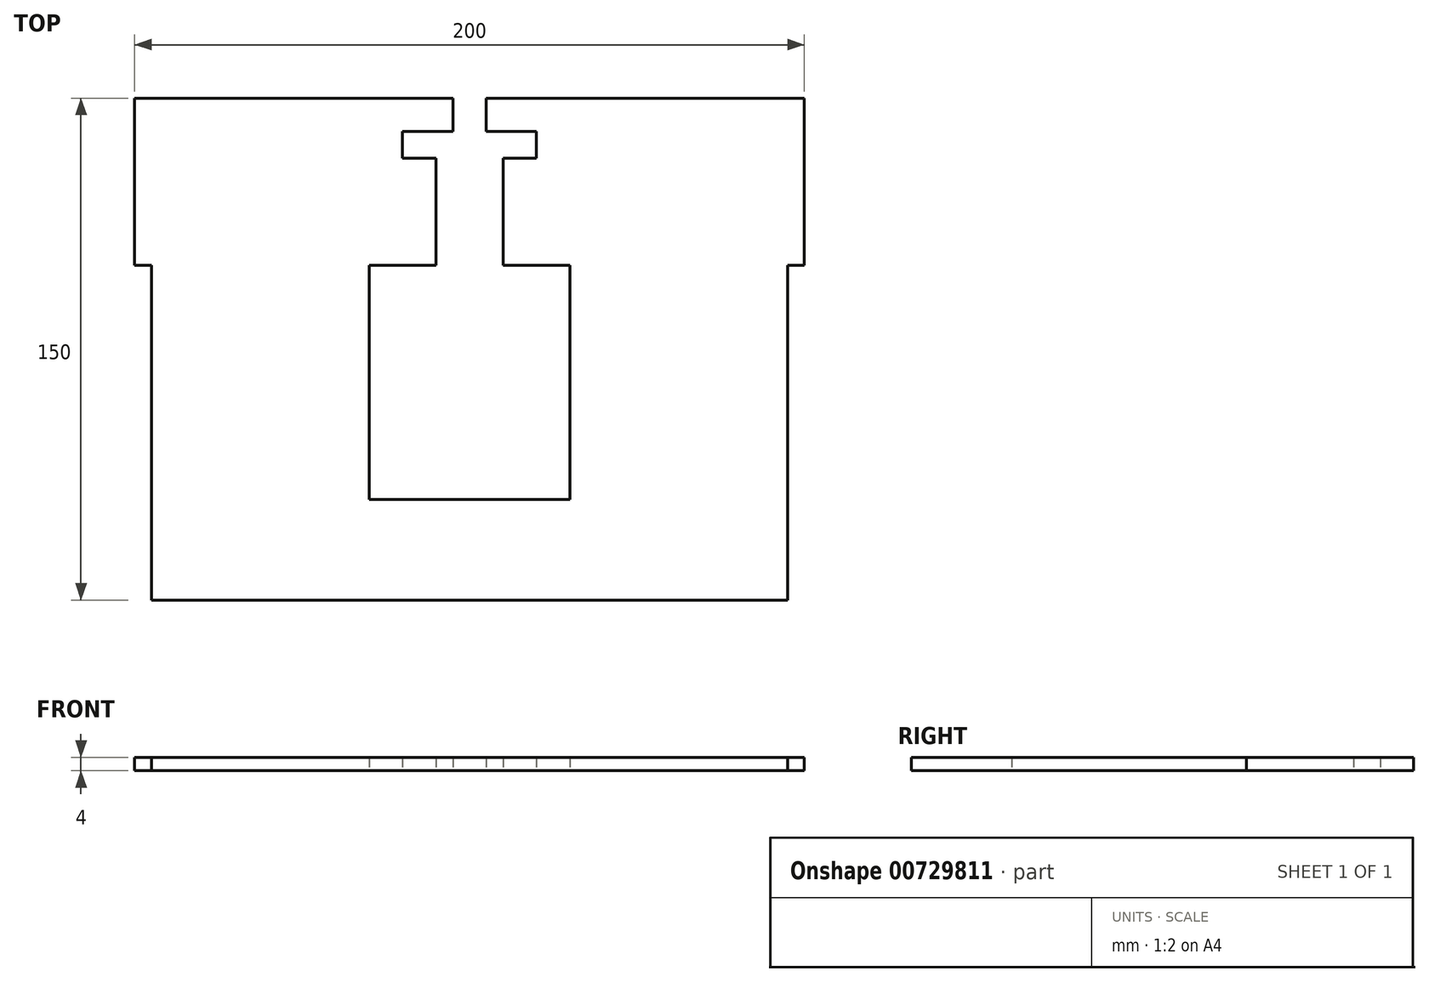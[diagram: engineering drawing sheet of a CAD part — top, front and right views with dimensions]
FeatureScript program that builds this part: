
annotation { "Feature Type Name" : "Feature", "Feature Type Description" : "" }
export const myFeature = defineFeature(function(context is Context, id is Id, definition is map)
    precondition{}
    {
        {
            var Q0;
            Q0=qCreatedBy(makeId("Top.planeOp"),FACE);
            var sketch = newSketch(context, id + "F0", { "sketchPlane" : qUnion([Q0])});
            skLineSegment(sketch, "E0.bottom", {"start": v(20, -10) * mm, "end": v(5, -10) * mm});
            skLineSegment(sketch, "E0.left", {"start": v(20, -10) * mm, "end": v(20, -18) * mm});
            skLineSegment(sketch, "E0.right", {"start": v(-20, -10) * mm, "end": v(-20, -18) * mm});
            skPoint(sketch, "E0.middle", {"position": v(0, 0) * mm});
            skLineSegment(sketch, "E1.top", {"start": v(-100, 0) * mm, "end": v(-5, 0) * mm});
            skLineSegment(sketch, "E1.left", {"start": v(-100, -50) * mm, "end": v(-100, 0) * mm});
            skLineSegment(sketch, "E1.right", {"start": v(100, -50) * mm, "end": v(100, 0) * mm});
            skLineSegment(sketch, "E2", {"start": v(-30, -50) * mm, "end": v(-30, -120) * mm});
            skLineSegment(sketch, "E3", {"start": v(30, -50) * mm, "end": v(30, -120) * mm});
            skLineSegment(sketch, "E4", {"start": v(20, -18) * mm, "end": v(10, -18) * mm});
            skLineSegment(sketch, "E5", {"start": v(10, -18) * mm, "end": v(10, -50) * mm});
            skLineSegment(sketch, "E6", {"start": v(-20, -18) * mm, "end": v(-10, -18) * mm});
            skLineSegment(sketch, "E7", {"start": v(-10, -18) * mm, "end": v(-10, -50) * mm});
            skLineSegment(sketch, "E8", {"start": v(30, -50) * mm, "end": v(10, -50) * mm});
            skLineSegment(sketch, "E9", {"start": v(-10, -50) * mm, "end": v(-30, -50) * mm});
            skLineSegment(sketch, "E10", {"start": v(0, 0) * mm, "end": v(0, -10) * mm, "construction": true});
            skLineSegment(sketch, "E11", {"start": v(95, -150) * mm, "end": v(-95, -150) * mm});
            skLineSegment(sketch, "E12", {"start": v(30, -120) * mm, "end": v(-30, -120) * mm});
            skLineSegment(sketch, "E13", {"start": v(0, -120) * mm, "end": v(0, -150) * mm, "construction": true});
            skLineSegment(sketch, "E14", {"start": v(-100, -50) * mm, "end": v(-95, -50) * mm});
            skLineSegment(sketch, "E15", {"start": v(-95, -50) * mm, "end": v(-95, -150) * mm});
            skLineSegment(sketch, "E16", {"start": v(100, -50) * mm, "end": v(95, -50) * mm});
            skLineSegment(sketch, "E17", {"start": v(95, -50) * mm, "end": v(95, -150) * mm});
            skLineSegment(sketch, "E18", {"start": v(5, 0) * mm, "end": v(100, 0) * mm});
            skLineSegment(sketch, "E19", {"start": v(5, -10) * mm, "end": v(0, -10) * mm, "construction": true});
            skLineSegment(sketch, "E20", {"start": v(-5, 0) * mm, "end": v(5, 0) * mm, "construction": true});
            skLineSegment(sketch, "E21", {"start": v(-5, -10) * mm, "end": v(-20, -10) * mm});
            skLineSegment(sketch, "E22", {"start": v(5, 0) * mm, "end": v(5, -10) * mm});
            skLineSegment(sketch, "E23", {"start": v(-5, -10) * mm, "end": v(-5, 0) * mm});
            skLineSegment(sketch, "E24", {"start": v(0, -10) * mm, "end": v(-5, -10) * mm, "construction": true});
            skSolve(sketch);
        }
        {
            var Q0;
            Q0 = qSketchRegion(id + "F0", true);
            extrude(context, id + "F1", {"entities" : qUnion([Q0]), "depth" : 4 * mm, "offsetDistance" : 25 * mm});
        }
    });
